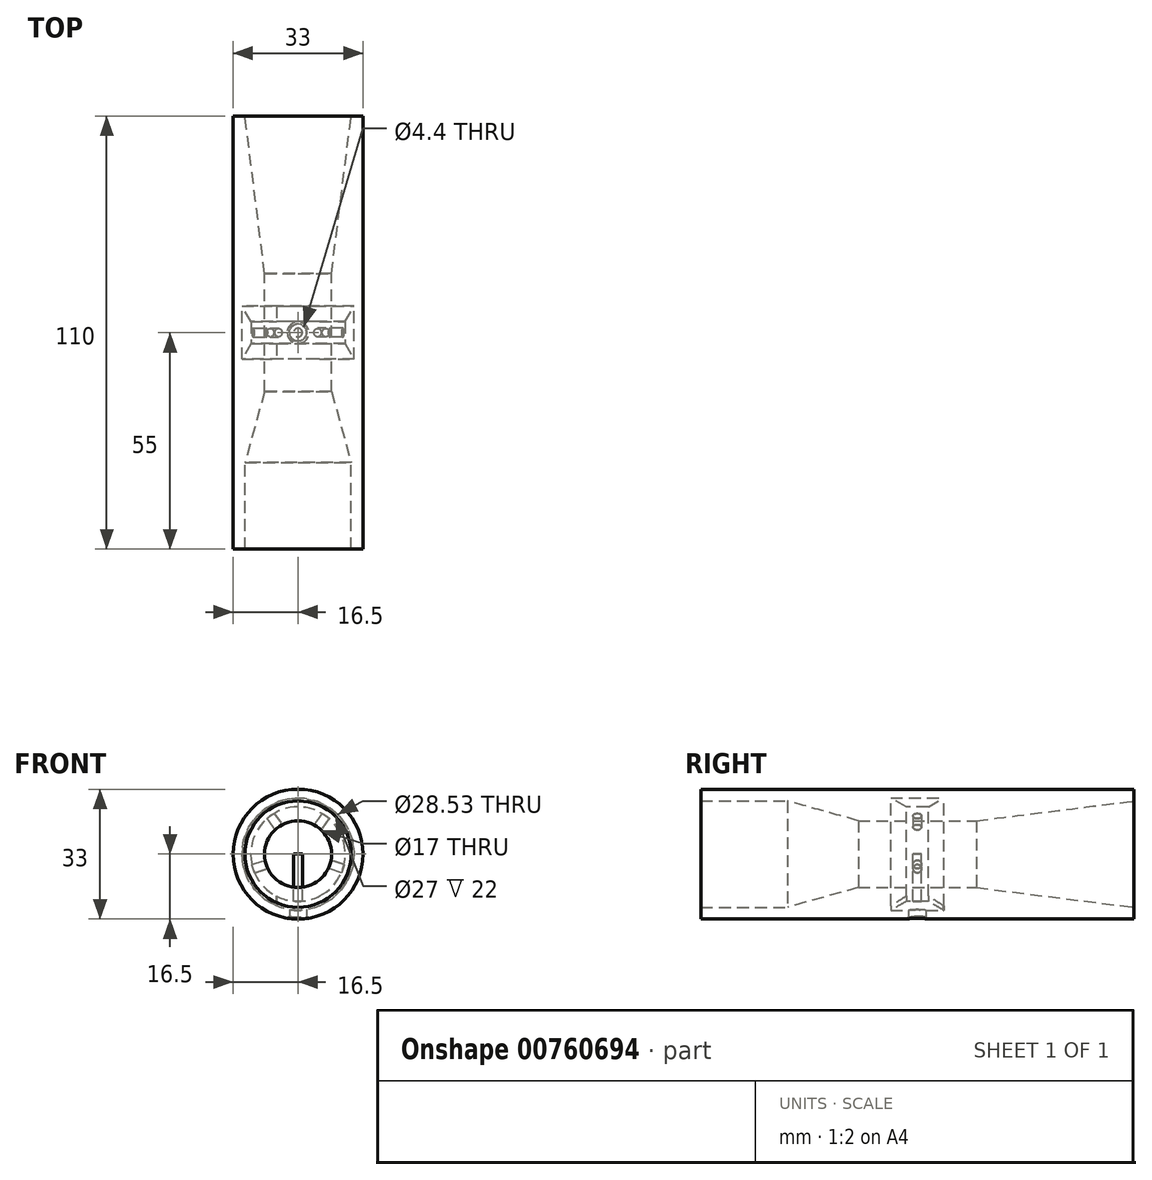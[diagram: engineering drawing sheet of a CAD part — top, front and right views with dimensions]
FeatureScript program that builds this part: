
annotation { "Feature Type Name" : "Feature", "Feature Type Description" : "" }
export const myFeature = defineFeature(function(context is Context, id is Id, definition is map)
    precondition{}
    {
        {
            var Q0;
            Q0=qCreatedBy(makeId("Front.planeOp"),FACE);
            var sketch = newSketch(context, id + "F0", { "sketchPlane" : qUnion([Q0])});
            skCircle(sketch, "E0", {"center": v(0, 0) * mm, "radius": 13.5 * mm});
            skCircle(sketch, "E1", {"center": v(0, 0) * mm, "radius": 16.5 * mm});
            skCircle(sketch, "E2", {"center": v(0, 0) * mm, "radius": 23.5 * mm});
            skCircle(sketch, "E3", {"center": v(0, 0) * mm, "radius": 26.5 * mm});
            skSolve(sketch);
        }
        {
            var Q0;
            Q0=qCreatedBy(makeId("Right.planeOp"),FACE);
            var sketch = newSketch(context, id + "F1", { "sketchPlane" : qUnion([Q0])});
            skLineSegment(sketch, "E4", {"start": v(0, 0) * mm, "end": v(0, 57.21) * mm, "construction": true});
            skLineSegment(sketch, "E5", {"start": v(15, 32.18) * mm, "end": v(15, -25.03) * mm, "construction": true});
            skLineSegment(sketch, "E6", {"start": v(55, 32.18) * mm, "end": v(55, -25.03) * mm, "construction": true});
            skLineSegment(sketch, "E7", {"start": v(55, 13.5) * mm, "end": v(-55, 13.5) * mm});
            skLineSegment(sketch, "E8", {"start": v(-15, 31.27) * mm, "end": v(-15, -25.94) * mm, "construction": true});
            skLineSegment(sketch, "E9", {"start": v(-55, 31.87) * mm, "end": v(-55, -25.34) * mm, "construction": true});
            skPoint(sketch, "E10", {"position": v(-33, 13.5) * mm});
            skLineSegment(sketch, "E11", {"start": v(-15, 8.5) * mm, "end": v(15, 8.5) * mm});
            skLineSegment(sketch, "E12", {"start": v(-15, 8.5) * mm, "end": v(-33, 13.5) * mm});
            skLineSegment(sketch, "E13", {"start": v(15, 8.5) * mm, "end": v(55, 13.5) * mm});
            skLineSegment(sketch, "E14", {"start": v(-32.07, 13.24) * mm, "end": v(-32.07, 0) * mm});
            skLineSegment(sketch, "E15", {"start": v(-32.07, 0) * mm, "end": v(48.4, 0) * mm});
            skLineSegment(sketch, "E16", {"start": v(48.4, 0) * mm, "end": v(48.4, 12.68) * mm});
            skLineSegment(sketch, "E17.MirrorCS", {"start": v(-15, -8.5) * mm, "end": v(15, -8.5) * mm, "construction": true});
            skLineSegment(sketch, "E18.MirrorCS", {"start": v(55, -13.5) * mm, "end": v(-55, -13.5) * mm, "construction": true});
            skLineSegment(sketch, "E19.bottom", {"start": v(10.63, -16.5) * mm, "end": v(-10.62, -16.5) * mm});
            skLineSegment(sketch, "E19.top", {"start": v(10.63, -7.75) * mm, "end": v(-10.62, -7.75) * mm});
            skLineSegment(sketch, "E19.left", {"start": v(10.63, -16.5) * mm, "end": v(10.63, -7.75) * mm});
            skLineSegment(sketch, "E19.right", {"start": v(-10.62, -16.5) * mm, "end": v(-10.62, -7.75) * mm});
            skPoint(sketch, "E19.middle", {"position": v(0, -12.13) * mm});
            skLineSegment(sketch, "E20", {"start": v(0, 0) * mm, "end": v(0, -13.5) * mm, "construction": true});
            skSolve(sketch);
        }
        {
            var Q0;
            Q0=makeQuery(id+"F0.imprint","IMPRINT",FACE,{"disambiguationData":[TD([[makeQuery(id+"F0.imprint","IMPRINT",EDGE,{"derivedFrom":sQuery(id+"F0.wireOp",EDGE,"E0")}),-1.0]])]});
            var Q1;
            Q1=sQuery(id+"F1.wireOp",VERTEX,"E7.end");
            extrude(context, id + "F2", {"entities" : qUnion([Q0]), "endBound" : BoundingType.UP_TO_VERTEX, "depth" : 60 * mm, "endBoundEntityVertex" : qUnion([Q1]), "offsetDistance" : 25 * mm});
        }
        {
            var Q0;
            Q0=makeQuery(id+"F2.opExtrude","CAP_FACE",FACE,{"disambiguationData":[OSD([sQuery(id+"F0.wireOp",EDGE,"E0"),sQuery(id+"F0.wireOp",EDGE,"E1")])],"isStart":true});
            var Q1;
            Q1=sQuery(id+"F1.wireOp",VERTEX,"E7.start");
            extrude(context, id + "F3", {"entities" : qUnion([Q0]), "operationType" : NewBodyOperationType.ADD, "endBound" : BoundingType.UP_TO_VERTEX, "depth" : 25 * mm, "endBoundEntityVertex" : qUnion([Q1]), "offsetDistance" : 25 * mm});
        }
        {
            var Q0;
            Q0=makeQuery(id+"F1.imprint","IMPRINT",FACE,{"disambiguationData":[TD([[makeQuery(id+"F1.imprint","IMPRINT",EDGE,{"derivedFrom":sQuery(id+"F1.wireOp",EDGE,"E11")}),1.0]])]});
            var Q1;
            {var subQ0=sQuery(id+"F0.wireOp",EDGE,"E0");Q1=makeQuery(id+"F3.boolean.opBoolean","MERGE",FACE,{"derivedFrom":[makeQuery(id+"F2.opExtrude","SWEPT_FACE",FACE,{"disambiguationData":[OSD([subQ0])]}),makeQuery(id+"F3.opExtrude","SWEPT_FACE",FACE,{"disambiguationData":[OSD([subQ0])]})]});}
            revolve(context, id + "F4", {"operationType" : NewBodyOperationType.ADD, "entities" : qUnion([Q0]), "axis" : qUnion([Q1]), "revolveType" : RevolveType.FULL});
        }
        {
            var Q0;
            Q0=qCreatedBy(makeId("Front.planeOp"),FACE);
            var Q1;
            Q1=sQuery(id+"F1.wireOp",VERTEX,"E11.start");
            cPlane(context, id + "F5", {"entities" : qUnion([Q0, Q1]), "cplaneType" : CPlaneType.PLANE_POINT, "offset" : 18 * mm, "width" : 150 * mm, "height" : 150 * mm});
        }
        {
            var Q0;
            Q0=qCreatedBy(makeId("Front.planeOp"),FACE);
            var Q1;
            Q1=sQuery(id+"F1.wireOp",VERTEX,"E11.end");
            cPlane(context, id + "F6", {"entities" : qUnion([Q0, Q1]), "cplaneType" : CPlaneType.PLANE_POINT, "offset" : 25 * mm, "width" : 150 * mm, "height" : 150 * mm});
        }
        {
            var Q0;
            Q0=qCreatedBy(makeId("Front.planeOp"),FACE);
            var sketch = newSketch(context, id + "F7", { "sketchPlane" : qUnion([Q0])});
            skCircle(sketch, "E21", {"center": v(0, 0) * mm, "radius": 12 * mm});
            skCircle(sketch, "E22", {"center": v(0, 0) * mm, "radius": 17.5 * mm});
            skSolve(sketch);
        }
        {
            var Q0;
            Q0=makeQuery(id+"F7.imprint","IMPRINT",FACE,{"disambiguationData":[TD([[makeQuery(id+"F7.imprint","IMPRINT",EDGE,{"derivedFrom":sQuery(id+"F7.wireOp",EDGE,"E21")}),-1.0]])]});
            extrude(context, id + "F8", {"entities" : qUnion([Q0]), "operationType" : NewBodyOperationType.REMOVE, "endBound" : BoundingType.SYMMETRIC, "oppositeDirection" : true, "depth" : 21.2 * mm, "offsetDistance" : 25 * mm});
        }
        {
            var Q0;
            Q0=qCreatedBy(makeId("Top.planeOp"),FACE);
            var sketch = newSketch(context, id + "F9", { "sketchPlane" : qUnion([Q0])});
            skCircle(sketch, "E23", {"center": v(0, 0) * mm, "radius": 2.2 * mm});
            skCircle(sketch, "E24", {"center": v(0, 0) * mm, "radius": 3.4 * mm});
            skCircle(sketch, "E25", {"center": v(0, 0) * mm, "radius": 1.1 * mm});
            skSolve(sketch);
        }
        {
            var Q0;
            Q0=makeQuery(id+"F9.imprint","IMPRINT",FACE,{"disambiguationData":[TD([[makeQuery(id+"F9.imprint","IMPRINT",EDGE,{"derivedFrom":sQuery(id+"F9.wireOp",EDGE,"E23")}),1.0]])]});
            var Q1;
            Q1=sQuery(id+"F9.wireOp",EDGE,"E23");
            extrude(context, id + "F10", {"entities" : qUnion([Q0]), "operationType" : NewBodyOperationType.REMOVE, "surfaceEntities" : qUnion([Q1]), "oppositeDirection" : true, "depth" : 120 * mm, "offsetDistance" : 25 * mm});
        }
        {
            var Q0;
            Q0=makeQuery(id+"F9.imprint","IMPRINT",FACE,{"disambiguationData":[TD([[makeQuery(id+"F9.imprint","IMPRINT",EDGE,{"derivedFrom":sQuery(id+"F9.wireOp",EDGE,"E23")}),-1.0]])]});
            extrude(context, id + "F11", {"entities" : qUnion([Q0]), "operationType" : NewBodyOperationType.ADD, "oppositeDirection" : true, "depth" : 21.4 * mm, "offsetDistance" : 25 * mm});
        }
        {
            var Q0;
            Q0=makeQuery(id+"F11.boolean.opBoolean","INTERSECT",EDGE,{"derivedFrom":[makeQuery(id+"F8.boolean.opBoolean","COPY",FACE,{"derivedFrom":makeQuery(id+"F8.opExtrude","SWEPT_FACE",FACE,{"disambiguationData":[OSD([sQuery(id+"F7.wireOp",EDGE,"E21")])]})}),makeQuery(id+"F11.opExtrude","SWEPT_FACE",FACE,{"disambiguationData":[OSD([sQuery(id+"F9.wireOp",EDGE,"E24")])]})]});
            fillet(context, id + "F12", {"entities" : qUnion([Q0]), "radius" : 2 * mm, "tangentPropagation" : true, "allowEdgeOverflow" : false});
        }
        {
            var Q0;
            Q0=makeQuery(id+"F11.opExtrude","CAP_FACE",FACE,{"disambiguationData":[OSD([sQuery(id+"F9.wireOp",EDGE,"E23"),sQuery(id+"F9.wireOp",EDGE,"E24")])],"isStart":false});
            var sketch = newSketch(context, id + "F13", { "sketchPlane" : qUnion([Q0])});
            skCircle(sketch, "E26", {"center": v(0, 0) * mm, "radius": 5.5 * mm});
            skSolve(sketch);
        }
        {
            var Q0;
            Q0=makeQuery(id+"F13.imprint","IMPRINT",FACE,{"disambiguationData":[TD([[makeQuery(id+"F13.imprint","IMPRINT",EDGE,{"derivedFrom":sQuery(id+"F13.wireOp",EDGE,"E26")}),1.0]])]});
            extrude(context, id + "F14", {"entities" : qUnion([Q0]), "operationType" : NewBodyOperationType.ADD, "endBound" : BoundingType.UP_TO_NEXT, "oppositeDirection" : true, "depth" : 25 * mm, "offsetDistance" : 25 * mm});
        }
        {
            var Q0;
            Q0=makeQuery(id+"F8.boolean.opBoolean","COPY",EDGE,{"derivedFrom":makeQuery(id+"F8.opExtrude","CAP_EDGE",EDGE,{"disambiguationData":[OSD([sQuery(id+"F7.wireOp",EDGE,"E21")])],"isStart":true})});
            var Q1;
            Q1=makeQuery(id+"F8.boolean.opBoolean","COPY",EDGE,{"derivedFrom":makeQuery(id+"F8.opExtrude","CAP_EDGE",EDGE,{"disambiguationData":[OSD([sQuery(id+"F7.wireOp",EDGE,"E21")])],"isStart":false})});
            chamfer(context, id + "F15", {"entities" : qUnion([Q0, Q1]), "chamferType" : ChamferType.OFFSET_ANGLE, "width" : 4.5 * mm, "oppositeDirection" : false, "angle" : 60 * degree, "tangentPropagation" : true});
        }
        {
            var Q0;
            {var subQ0=sQuery(id+"F9.wireOp",EDGE,"E24");Q0=makeQuery(id+"F14.boolean.opBoolean","MERGE",FACE,{"derivedFrom":[makeQuery(id+"F11.opExtrude","CAP_FACE",FACE,{"disambiguationData":[OSD([sQuery(id+"F9.wireOp",EDGE,"E23"),subQ0])],"isStart":false}),makeQuery(id+"F14.opExtrude","CAP_FACE",FACE,{"disambiguationData":[OSD([subQ0,sQuery(id+"F13.wireOp",EDGE,"E26")])],"isStart":true})]});}
            extrude(context, id + "F16", {"entities" : qUnion([Q0]), "operationType" : NewBodyOperationType.REMOVE, "oppositeDirection" : true, "depth" : 4.85 * mm, "offsetDistance" : 25 * mm});
        }
        {
            var Q0;
            Q0=makeQuery(id+"F1.imprint","IMPRINT",FACE,{"disambiguationData":[TD([[makeQuery(id+"F1.imprint","IMPRINT",EDGE,{"derivedFrom":sQuery(id+"F1.wireOp",EDGE,"E19.bottom")}),-1.0]])]});
            extrude(context, id + "F17", {"entities" : qUnion([Q0]), "operationType" : NewBodyOperationType.ADD, "endBound" : BoundingType.SYMMETRIC, "depth" : 11.04 * mm, "offsetDistance" : 25 * mm});
        }
        {
            var Q0;
            Q0=makeQuery(id+"F2.opExtrude","CAP_FACE",FACE,{"disambiguationData":[OSD([sQuery(id+"F0.wireOp",EDGE,"E0"),sQuery(id+"F0.wireOp",EDGE,"E1")])],"isStart":false});
            var sketch = newSketch(context, id + "F18", { "sketchPlane" : qUnion([Q0])});
            skCircle(sketch, "E27", {"center": v(0, 0) * mm, "radius": 26.69 * mm});
            skSolve(sketch);
        }
        {
            var Q0;
            Q0=makeQuery(id+"F18.imprint","IMPRINT",FACE,{"disambiguationData":[TD([[makeQuery(id+"F18.imprint","IMPRINT",EDGE,{"derivedFrom":sQuery(id+"F18.wireOp",EDGE,"E27")}),1.0]])]});
            var Q1;
            Q1=makeQuery(id+"F3.opExtrude","CAP_FACE",FACE,{"disambiguationData":[OSD([sQuery(id+"F0.wireOp",EDGE,"E0"),sQuery(id+"F0.wireOp",EDGE,"E1")])],"isStart":false});
            extrude(context, id + "F19", {"entities" : qUnion([Q0]), "operationType" : NewBodyOperationType.REMOVE, "endBound" : BoundingType.UP_TO_SURFACE, "oppositeDirection" : true, "depth" : 25 * mm, "endBoundEntityFace" : qUnion([Q1]), "offsetDistance" : 25 * mm});
        }
        {
            var Q0;
            {var subQ1=sQuery(id+"F1.wireOp",EDGE,"E11");Q0=makeQuery(id+"F1.imprint","IMPRINT",FACE,{"disambiguationData":[TD([[makeQuery(id+"F1.imprint","IMPRINT",EDGE,{"derivedFrom":subQ1}),-1.0]])]});}
            var Q1;
            Q1=makeQuery(id+"F4.opRevolve","SWEPT_FACE",FACE,{"disambiguationData":[OSD([sQuery(id+"F1.wireOp",EDGE,"E11")])]});
            revolve(context, id + "F20", {"operationType" : NewBodyOperationType.REMOVE, "surfaceOperationType" : NewSurfaceOperationType.NEW, "entities" : qUnion([Q0]), "axis" : qUnion([Q1]), "revolveType" : RevolveType.FULL, "oppositeDirection" : true});
        }
        {
            var Q0;
            Q0=makeQuery(id+"F9.imprint","IMPRINT",FACE,{"disambiguationData":[TD([[makeQuery(id+"F9.imprint","IMPRINT",EDGE,{"derivedFrom":sQuery(id+"F9.wireOp",EDGE,"E23")}),1.0]])]});
            var Q1;
            {var subQ1=sQuery(id+"F7.wireOp",EDGE,"E21");Q1=makeQuery(id+"F10.boolean.opBoolean","SPLIT",FACE,{"disambiguationData":[TD([makeQuery(id+"F10.opExtrude","SWEPT_FACE",FACE,{"disambiguationData":[OSD([sQuery(id+"F9.wireOp",EDGE,"E23")])]})])],"derivedFrom":makeQuery(id+"F8.boolean.opBoolean","COPY",FACE,{"derivedFrom":makeQuery(id+"F8.opExtrude","SWEPT_FACE",FACE,{"disambiguationData":[OSD([subQ1])]})})});}
            extrude(context, id + "F21", {"entities" : qUnion([Q0]), "endBound" : BoundingType.UP_TO_SURFACE, "oppositeDirection" : true, "depth" : 22.7 * mm, "endBoundEntityFace" : qUnion([Q1]), "offsetDistance" : 25 * mm});
        }
        {
            var Q0;
            Q0=makeQuery(id+"F9.imprint","IMPRINT",FACE,{"disambiguationData":[TD([[makeQuery(id+"F9.imprint","IMPRINT",EDGE,{"derivedFrom":sQuery(id+"F9.wireOp",EDGE,"E25")}),1.0]])]});
            var Q1;
            {var subQ1=sQuery(id+"F7.wireOp",EDGE,"E21");Q1=makeQuery(id+"F10.boolean.opBoolean","SPLIT",FACE,{"disambiguationData":[TD([makeQuery(id+"F10.opExtrude","SWEPT_FACE",FACE,{"disambiguationData":[OSD([sQuery(id+"F9.wireOp",EDGE,"E23")])]})])],"derivedFrom":makeQuery(id+"F8.boolean.opBoolean","COPY",FACE,{"derivedFrom":makeQuery(id+"F8.opExtrude","SWEPT_FACE",FACE,{"disambiguationData":[OSD([subQ1])]})})});}
            extrude(context, id + "F22", {"entities" : qUnion([Q0]), "endBound" : BoundingType.UP_TO_SURFACE, "oppositeDirection" : true, "depth" : 25 * mm, "endBoundEntityFace" : qUnion([Q1]), "offsetDistance" : 25 * mm});
        }
        {
            var Q0;
            Q0=makeQuery(id+"F21.opExtrude","SWEPT_BODY",BODY,{"disambiguationData":[OSD([sQuery(id+"F9.wireOp",EDGE,"E23"),sQuery(id+"F9.wireOp",EDGE,"E25")])]});
            deleteBodies(context, id + "F23", {"entities" : qUnion([Q0])});
        }
        {
            var Q0;
            Q0=makeQuery(id+"F22.opExtrude","SWEPT_BODY",BODY,{"disambiguationData":[OSD([sQuery(id+"F9.wireOp",EDGE,"E25")])]});
            var Q1;
            Q1=sQuery(id+"F1.wireOp",EDGE,"E15");
            circularPattern(context, id + "F24", {"entities" : qUnion([Q0]), "axis" : qUnion([Q1]), "angle" : 360 * degree, "instanceCount" : 5, "equalSpace" : true});
        }
        {
            var Q0;
            Q0=makeQuery(id+"F17.opExtrude","CAP_FACE",FACE,{"disambiguationData":[OSD([sQuery(id+"F1.wireOp",EDGE,"E19.bottom"),sQuery(id+"F1.wireOp",EDGE,"E19.top"),sQuery(id+"F1.wireOp",EDGE,"E19.left"),sQuery(id+"F1.wireOp",EDGE,"E19.right")])],"isStart":false});
            var sketch = newSketch(context, id + "F25", { "sketchPlane" : qUnion([Q0])});
            skLineSegment(sketch, "E28", {"start": v(-2.8, -10.66) * mm, "end": v(-6.73, -13.16) * mm});
            skLineSegment(sketch, "E29", {"start": v(-6.73, -13.16) * mm, "end": v(6.73, -13.16) * mm});
            skLineSegment(sketch, "E30", {"start": v(6.73, -13.16) * mm, "end": v(2.8, -10.66) * mm});
            skLineSegment(sketch, "E31", {"start": v(2.8, -10.66) * mm, "end": v(-2.8, -10.66) * mm});
            skSolve(sketch);
        }
        {
            var Q0;
            {var subQ2=sQuery(id+"F25.wireOp",EDGE,"E29");Q0=makeQuery(id+"F25.imprint","IMPRINT",FACE,{"disambiguationData":[TD([[makeQuery(id+"F25.imprint","IMPRINT",EDGE,{"derivedFrom":subQ2}),1.0]])]});}
            var Q1;
            Q1=sQuery(id+"F1.wireOp",EDGE,"E15");
            revolve(context, id + "F26", {"operationType" : NewBodyOperationType.REMOVE, "surfaceOperationType" : NewSurfaceOperationType.NEW, "entities" : qUnion([Q0]), "axis" : qUnion([Q1]), "revolveType" : RevolveType.FULL, "oppositeDirection" : true});
        }
        {
            var Q0;
            Q0=makeQuery(id+"F24.opPattern","COPY",BODY,{"derivedFrom":makeQuery(id+"F22.opExtrude","SWEPT_BODY",BODY,{"disambiguationData":[OSD([sQuery(id+"F9.wireOp",EDGE,"E25")])]}),"instanceName":"1"});
            var Q1;
            Q1=makeQuery(id+"F24.opPattern","COPY",BODY,{"derivedFrom":makeQuery(id+"F22.opExtrude","SWEPT_BODY",BODY,{"disambiguationData":[OSD([sQuery(id+"F9.wireOp",EDGE,"E25")])]}),"instanceName":"2"});
            var Q2;
            Q2=makeQuery(id+"F24.opPattern","COPY",BODY,{"derivedFrom":makeQuery(id+"F22.opExtrude","SWEPT_BODY",BODY,{"disambiguationData":[OSD([sQuery(id+"F9.wireOp",EDGE,"E25")])]}),"instanceName":"3"});
            var Q3;
            Q3=makeQuery(id+"F24.opPattern","COPY",BODY,{"derivedFrom":makeQuery(id+"F22.opExtrude","SWEPT_BODY",BODY,{"disambiguationData":[OSD([sQuery(id+"F9.wireOp",EDGE,"E25")])]}),"instanceName":"4"});
            var Q4;
            Q4=makeQuery(id+"F10.boolean.opBoolean","SPLIT",BODY,{"disambiguationData":[OD(0.0)],"derivedFrom":makeQuery(id+"F2.opExtrude","SWEPT_BODY",BODY,{"disambiguationData":[OSD([sQuery(id+"F0.wireOp",EDGE,"E0"),sQuery(id+"F0.wireOp",EDGE,"E1")])]})});
            booleanBodies(context, id + "F27", {"operationType" : BooleanOperationType.SUBTRACTION, "tools" : qUnion([Q0, Q1, Q2, Q3]), "targets" : qUnion([Q4])});
        }
        {
            var Q0;
            Q0=qCreatedBy(makeId("Top.planeOp"),FACE);
            cPlane(context, id + "F28", {"entities" : qUnion([Q0]), "cplaneType" : CPlaneType.OFFSET, "offset" : 25 * mm, "oppositeDirection" : true, "width" : 150 * mm, "height" : 150 * mm});
        }
        {
            var Q0;
            Q0=makeQuery(id+"F17.opExtrude","CAP_FACE",FACE,{"disambiguationData":[OSD([sQuery(id+"F1.wireOp",EDGE,"E19.bottom"),sQuery(id+"F1.wireOp",EDGE,"E19.top"),sQuery(id+"F1.wireOp",EDGE,"E19.left"),sQuery(id+"F1.wireOp",EDGE,"E19.right")])],"isStart":true});
            var Q1;
            Q1=sQuery(id+"F1.wireOp",EDGE,"E15");
            revolve(context, id + "F29", {"operationType" : NewBodyOperationType.ADD, "surfaceOperationType" : NewSurfaceOperationType.NEW, "entities" : qUnion([Q0]), "axis" : qUnion([Q1]), "revolveType" : RevolveType.FULL});
        }
        {
            var Q0;
            Q0=qCreatedBy(id+"F28.planeOp",FACE);
            var sketch = newSketch(context, id + "F30", { "sketchPlane" : qUnion([Q0])});
            skCircle(sketch, "E32", {"center": v(0, 0) * mm, "radius": 2.2 * mm});
            skSolve(sketch);
        }
        {
            var Q0;
            Q0=makeQuery(id+"F30.imprint","IMPRINT",FACE,{"disambiguationData":[TD([[makeQuery(id+"F30.imprint","IMPRINT",EDGE,{"derivedFrom":sQuery(id+"F30.wireOp",EDGE,"E32")}),1.0]])]});
            var Q1;
            Q1=makeQuery(id+"F26.boolean.opBoolean","COPY",FACE,{"derivedFrom":makeQuery(id+"F26.opRevolve","SWEPT_FACE",FACE,{"disambiguationData":[OSD([sQuery(id+"F25.wireOp",EDGE,"E29")])]})});
            extrude(context, id + "F31", {"entities" : qUnion([Q0]), "operationType" : NewBodyOperationType.REMOVE, "endBound" : BoundingType.UP_TO_SURFACE, "depth" : 25 * mm, "endBoundEntityFace" : qUnion([Q1]), "offsetDistance" : 25 * mm});
        }
        {
            var Q0;
            {var subQ0=sQuery(id+"F0.wireOp",EDGE,"E1");var subQ1=sQuery(id+"F0.wireOp",EDGE,"E0");var subQ4=makeQuery(id+"F3.boolean.opBoolean","MERGE",FACE,{"derivedFrom":[makeQuery(id+"F2.opExtrude","SWEPT_FACE",FACE,{"disambiguationData":[OSD([subQ0])]}),makeQuery(id+"F3.opExtrude","SWEPT_FACE",FACE,{"disambiguationData":[OSD([subQ0])]})]});Q0=makeQuery(id+"F31.boolean.opBoolean","INTERSECT",EDGE,{"derivedFrom":[makeQuery(id+"F29.boolean.opBoolean","MERGE",FACE,{"derivedFrom":[makeQuery(id+"F19.boolean.opBoolean","MERGE",FACE,{"derivedFrom":[makeQuery(id+"F8.boolean.opBoolean","SPLIT",FACE,{"disambiguationData":[TD([makeQuery(id+"F2.opExtrude","CAP_FACE",FACE,{"disambiguationData":[OSD([subQ1,subQ0])],"isStart":false})])],"derivedFrom":subQ4}),makeQuery(id+"F8.boolean.opBoolean","SPLIT",FACE,{"disambiguationData":[TD([makeQuery(id+"F3.opExtrude","CAP_FACE",FACE,{"disambiguationData":[OSD([subQ1,subQ0])],"isStart":false})])],"derivedFrom":subQ4})],"fromTools":[makeQuery(id+"F19.opExtrude","SWEPT_FACE",FACE,{"disambiguationData":[OSD([subQ0])]})]}),makeQuery(id+"F29.opRevolve","SWEPT_FACE",FACE,{"disambiguationData":[OSD([subQ0,sQuery(id+"F1.wireOp",EDGE,"E19.bottom"),sQuery(id+"F1.wireOp",EDGE,"E19.top"),sQuery(id+"F1.wireOp",EDGE,"E19.left"),sQuery(id+"F1.wireOp",EDGE,"E19.right")])]})]}),makeQuery(id+"F31.opExtrude","SWEPT_FACE",FACE,{"disambiguationData":[OSD([sQuery(id+"F30.wireOp",EDGE,"E32")])]})]});}
            chamfer(context, id + "F32", {"entities" : qUnion([Q0]), "width" : 0.5 * mm, "tangentPropagation" : true});
        }
    });
